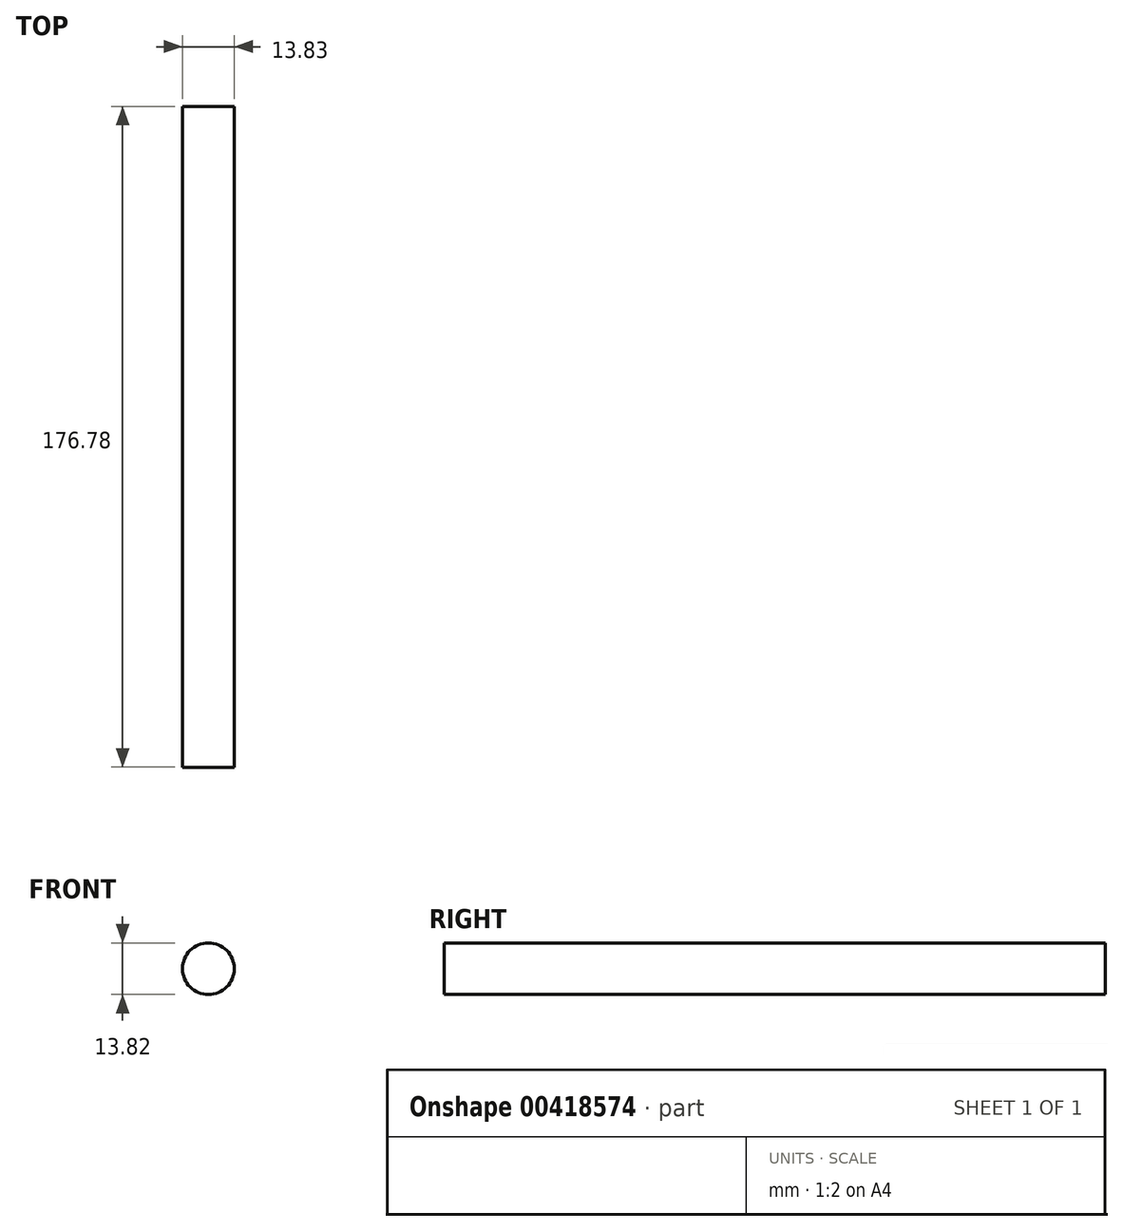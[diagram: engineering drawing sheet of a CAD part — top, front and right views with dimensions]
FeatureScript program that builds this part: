
annotation { "Feature Type Name" : "Feature", "Feature Type Description" : "" }
export const myFeature = defineFeature(function(context is Context, id is Id, definition is map)
    precondition{}
    {
        {
            var Q0;
            Q0=qCreatedBy(makeId("Front.planeOp"),FACE);
            var sketch = newSketch(context, id + "F0", { "sketchPlane" : qUnion([Q0])});
            skLineSegment(sketch, "E0", {"start": v(0, 11.04) * mm, "end": v(0, -14.36) * mm, "construction": true});
            skCircle(sketch, "E1", {"center": v(176.78, 0) * mm, "radius": 6.91 * mm});
            skSolve(sketch);
        }
        {
            var Q0;
            Q0=makeQuery(id+"F0.imprint","IMPRINT",FACE,{"disambiguationData":[TD([[makeQuery(id+"F0.imprint","IMPRINT",EDGE,{"derivedFrom":sQuery(id+"F0.wireOp",EDGE,"E1")}),1.0]])]});
            var Q1;
            Q1=sQuery(id+"F0.wireOp",EDGE,"E1");
            extrude(context, id + "F1", {"entities" : qUnion([Q0]), "bodyType" : ToolBodyType.SURFACE, "surfaceEntities" : qUnion([Q1]), "depth" : 176.78 * mm});
        }
    });
